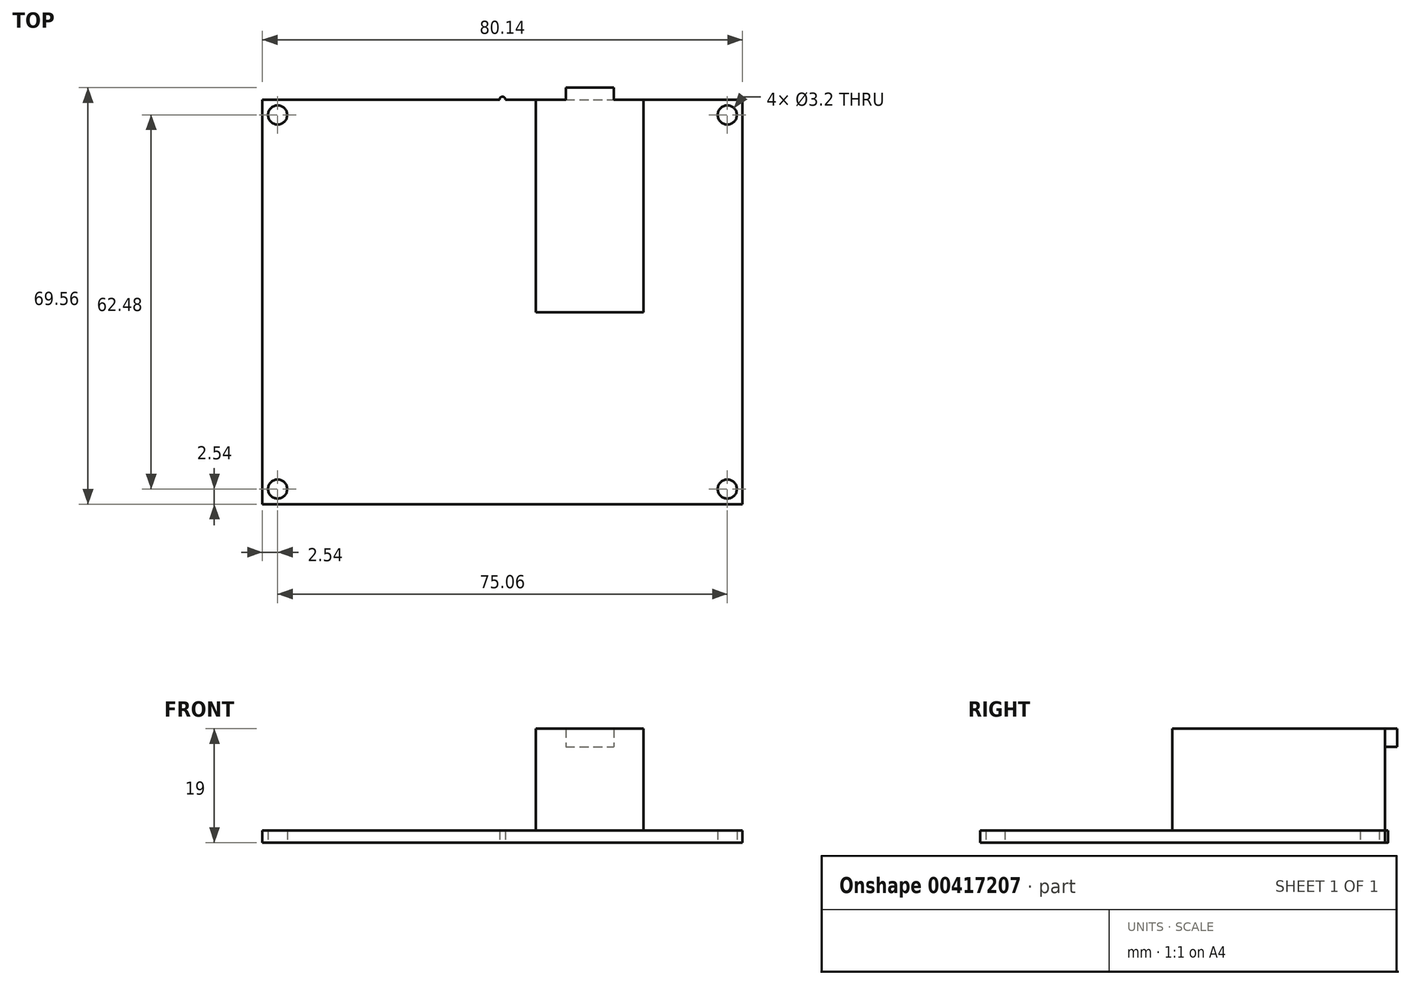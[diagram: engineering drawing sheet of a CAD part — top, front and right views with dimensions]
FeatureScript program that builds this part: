
annotation { "Feature Type Name" : "Feature", "Feature Type Description" : "" }
export const myFeature = defineFeature(function(context is Context, id is Id, definition is map)
    precondition{}
    {
        {
            var Q0;
            Q0=qCreatedBy(makeId("Top.planeOp"),FACE);
            var sketch = newSketch(context, id + "F0", { "sketchPlane" : qUnion([Q0])});
            skLineSegment(sketch, "E0.bottom", {"start": v(40.07, -33.78) * mm, "end": v(-40.07, -33.78) * mm});
            skLineSegment(sketch, "E0.top", {"start": v(40.07, 33.78) * mm, "end": v(-40.07, 33.78) * mm});
            skLineSegment(sketch, "E0.left", {"start": v(40.07, -33.78) * mm, "end": v(40.07, 33.78) * mm});
            skLineSegment(sketch, "E0.right", {"start": v(-40.07, -33.78) * mm, "end": v(-40.07, 33.78) * mm});
            skPoint(sketch, "E0.middle", {"position": v(0, 0) * mm});
            skCircle(sketch, "E1", {"center": v(-37.53, 31.24) * mm, "radius": 1.6 * mm});
            skCircle(sketch, "E2", {"center": v(37.53, 31.24) * mm, "radius": 1.6 * mm});
            skCircle(sketch, "E3", {"center": v(-37.53, -31.24) * mm, "radius": 1.6 * mm});
            skCircle(sketch, "E4", {"center": v(37.53, -31.24) * mm, "radius": 1.6 * mm});
            skCircle(sketch, "E5", {"center": v(0, 33.78) * mm, "radius": 0.5 * mm});
            skSolve(sketch);
        }
        {
            var Q0;
            Q0=qSketchRegion(id+"F0",true);
            extrude(context, id + "F1", {"entities" : qUnion([Q0]), "depth" : 2 * mm});
        }
        {
            var Q0;
            Q0=makeQuery(id+"F1.opExtrude","CAP_FACE",FACE,{"disambiguationData":[OSD([sQuery(id+"F0.wireOp",EDGE,"E0.bottom"),sQuery(id+"F0.wireOp",EDGE,"E0.top"),sQuery(id+"F0.wireOp",EDGE,"E0.left"),sQuery(id+"F0.wireOp",EDGE,"E0.right"),sQuery(id+"F0.wireOp",EDGE,"E1"),sQuery(id+"F0.wireOp",EDGE,"E2"),sQuery(id+"F0.wireOp",EDGE,"E3"),sQuery(id+"F0.wireOp",EDGE,"E4"),sQuery(id+"F0.wireOp",EDGE,"E5")])],"isStart":false});
            cPlane(context, id + "F2", {"entities" : qUnion([Q0]), "cplaneType" : CPlaneType.OFFSET, "offset" : 0 * mm, "width" : 150 * mm, "height" : 150 * mm});
        }
        {
            var Q0;
            Q0=qCreatedBy(id+"F2.planeOp",FACE);
            var sketch = newSketch(context, id + "F3", { "sketchPlane" : qUnion([Q0])});
            skLineSegment(sketch, "E6.0", {"start": v(40.07, 33.78) * mm, "end": v(0.5, 33.78) * mm, "construction": true});
            skLineSegment(sketch, "E7.0", {"start": v(40.07, -33.78) * mm, "end": v(40.07, 33.78) * mm, "construction": true});
            skCircle(sketch, "E8.0", {"center": v(37.53, 31.24) * mm, "radius": 1.6 * mm, "construction": true});
            skLineSegment(sketch, "E9.bottom", {"start": v(5.56, 33.78) * mm, "end": v(23.56, 33.78) * mm});
            skLineSegment(sketch, "E9.top", {"start": v(5.56, -1.72) * mm, "end": v(23.56, -1.72) * mm});
            skLineSegment(sketch, "E9.left", {"start": v(5.56, 33.78) * mm, "end": v(5.56, -1.72) * mm});
            skLineSegment(sketch, "E9.right", {"start": v(23.56, 33.78) * mm, "end": v(23.56, -1.72) * mm});
            skSolve(sketch);
        }
        {
            var Q0;
            Q0=qSketchRegion(id+"F3",true);
            extrude(context, id + "F4", {"entities" : qUnion([Q0]), "operationType" : NewBodyOperationType.ADD, "depth" : 17 * mm});
        }
        {
            var Q0;
            {var subQ0=sQuery(id+"F0.wireOp",EDGE,"E0.top");Q0=makeQuery(id+"F4.boolean.opBoolean","MERGE",FACE,{"derivedFrom":[makeQuery(id+"F1.opExtrude","SWEPT_FACE",FACE,{"disambiguationData":[OSD([subQ0]),TDD([makeQuery(id+"F0.imprint","IMPRINT",EDGE,{"disambiguationData":[TD([[makeQuery(id+"F0.imprint","INTERSECT",VERTEX,{"derivedFrom":[subQ0,sQuery(id+"F0.wireOp",EDGE,"E0.left")]}),-1.0]])],"derivedFrom":subQ0})])]}),makeQuery(id+"F4.opExtrude","SWEPT_FACE",FACE,{"disambiguationData":[OSD([sQuery(id+"F3.wireOp",EDGE,"E9.bottom")])]})]});}
            cPlane(context, id + "F5", {"entities" : qUnion([Q0]), "cplaneType" : CPlaneType.OFFSET, "offset" : 0 * mm, "width" : 150 * mm, "height" : 150 * mm});
        }
        {
            var Q0;
            Q0=qCreatedBy(id+"F5.planeOp",FACE);
            var sketch = newSketch(context, id + "F6", { "sketchPlane" : qUnion([Q0])});
            skLineSegment(sketch, "E10.0", {"start": v(-5.56, 19) * mm, "end": v(-5.56, 2) * mm, "construction": true});
            skLineSegment(sketch, "E11.0", {"start": v(-5.56, 19) * mm, "end": v(-23.56, 19) * mm, "construction": true});
            skLineSegment(sketch, "E12.0", {"start": v(-23.56, 19) * mm, "end": v(-23.56, 2) * mm, "construction": true});
            skLineSegment(sketch, "E13.bottom", {"start": v(-10.56, 19) * mm, "end": v(-18.56, 19) * mm});
            skLineSegment(sketch, "E13.top", {"start": v(-10.56, 16) * mm, "end": v(-18.56, 16) * mm});
            skLineSegment(sketch, "E13.left", {"start": v(-10.56, 19) * mm, "end": v(-10.56, 16) * mm});
            skLineSegment(sketch, "E13.right", {"start": v(-18.56, 19) * mm, "end": v(-18.56, 16) * mm});
            skSolve(sketch);
        }
        {
            var Q0;
            Q0=qSketchRegion(id+"F6",true);
            extrude(context, id + "F7", {"entities" : qUnion([Q0]), "operationType" : NewBodyOperationType.ADD, "depth" : 2 * mm});
        }
    });
